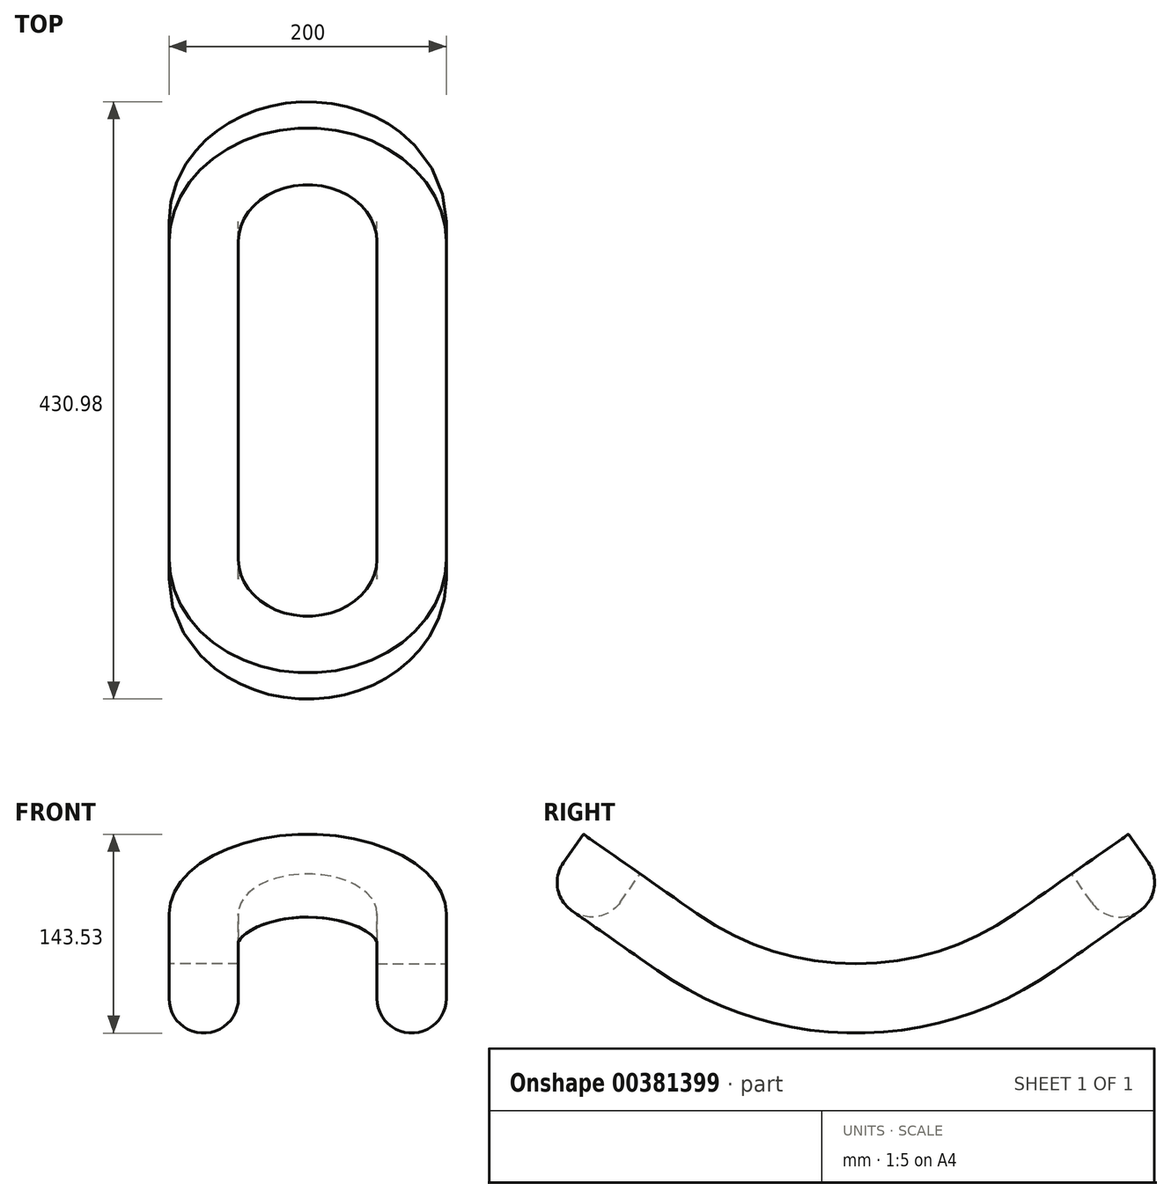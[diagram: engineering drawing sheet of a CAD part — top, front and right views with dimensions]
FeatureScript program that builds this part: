
annotation { "Feature Type Name" : "Feature", "Feature Type Description" : "" }
export const myFeature = defineFeature(function(context is Context, id is Id, definition is map)
    precondition{}
    {
        {
            var Q0;
            Q0=qCreatedBy(makeId("Right.planeOp"),FACE);
            var sketch = newSketch(context, id + "F0", { "sketchPlane" : qUnion([Q0])});
            skLineSegment(sketch, "E0", {"start": v(0, 0) * mm, "end": v(0, 200) * mm, "construction": true});
            skArc(sketch, "E1", {"start": v(0, 0) * mm, "mid": v(60.14, 9.26) * mm, "end": v(114.72, 36.17) * mm});
            skLineSegment(sketch, "E2", {"start": v(114.72, 36.17) * mm, "end": v(196.63, 93.53) * mm});
            skLineSegment(sketch, "E3", {"start": v(114.72, 36.17) * mm, "end": v(0, 200) * mm, "construction": true});
            skSolve(sketch);
        }
        {
            var Q0;
            Q0=sQuery(id+"F0.wireOp",EDGE,"E2");
            var Q1;
            Q1=sQuery(id+"F0.wireOp",EDGE,"E1");
            extrude(context, id + "F1", {"bodyType" : ToolBodyType.SURFACE, "surfaceEntities" : qUnion([Q0, Q1]), "depth" : 100 * mm});
        }
        {
            var Q0;
            Q0=makeQuery(id+"F1.opExtrude","SWEPT_FACE",FACE,{"disambiguationData":[OSD([sQuery(id+"F0.wireOp",EDGE,"E2")])]});
            var sketch = newSketch(context, id + "F2", { "sketchPlane" : qUnion([Q0])});
            skArc(sketch, "E4", {"start": v(0, -214.72) * mm, "mid": v(70.71, -185.43) * mm, "end": v(100, -114.72) * mm});
            skSolve(sketch);
        }
        {
            var Q0;
            Q0=qCreatedBy(makeId("Front.planeOp"),FACE);
            var sketch = newSketch(context, id + "F3", { "sketchPlane" : qUnion([Q0])});
            skLineSegment(sketch, "E5.bottom", {"start": v(50, 0) * mm, "end": v(100, 0) * mm});
            skLineSegment(sketch, "E5.top", {"start": v(50, -25) * mm, "end": v(100, -25) * mm, "construction": true});
            skLineSegment(sketch, "E5.left", {"start": v(50, 0) * mm, "end": v(50, -25) * mm});
            skLineSegment(sketch, "E5.right", {"start": v(100, 0) * mm, "end": v(100, -25) * mm});
            skArc(sketch, "E6", {"start": v(50, -25) * mm, "mid": v(75, -50) * mm, "end": v(100, -25) * mm});
            skSolve(sketch);
        }
        {
            var Q0;
            Q0=makeQuery(id+"F3.imprint","IMPRINT",FACE,{"disambiguationData":[TD([[makeQuery(id+"F3.imprint","IMPRINT",EDGE,{"derivedFrom":sQuery(id+"F3.wireOp",EDGE,"E5.bottom")}),-1.0]])]});
            var Q1;
            Q1=sQuery(id+"F2.wireOp",EDGE,"E4");
            var Q2;
            Q2=makeQuery(id+"F1.opExtrude","CAP_EDGE",EDGE,{"disambiguationData":[OSD([sQuery(id+"F0.wireOp",EDGE,"E1")])],"isStart":false});
            sweep(context, id + "F4", {"profiles" : qUnion([Q0]), "path" : qUnion([Q1, Q2])});
        }
        {
            var Q0;
            Q0=makeQuery(id+"F4.opSweep","SWEPT_BODY",BODY,{"disambiguationData":[OSD([sQuery(id+"F0.wireOp",EDGE,"E1"),sQuery(id+"F3.wireOp",EDGE,"E5.bottom"),sQuery(id+"F3.wireOp",EDGE,"E5.left"),sQuery(id+"F3.wireOp",EDGE,"E5.right"),sQuery(id+"F3.wireOp",EDGE,"E6")])]});
            var Q1;
            Q1=qCreatedBy(makeId("Right.planeOp"),FACE);
            mirror(context, id + "F5", {"operationType" : NewBodyOperationType.ADD, "entities" : qUnion([Q0]), "mirrorPlane" : qUnion([Q1])});
        }
        {
            var Q0;
            Q0=makeQuery(id+"F4.opSweep","SWEPT_BODY",BODY,{"disambiguationData":[OSD([sQuery(id+"F0.wireOp",EDGE,"E1"),sQuery(id+"F3.wireOp",EDGE,"E5.bottom"),sQuery(id+"F3.wireOp",EDGE,"E5.left"),sQuery(id+"F3.wireOp",EDGE,"E5.right"),sQuery(id+"F3.wireOp",EDGE,"E6")])]});
            var Q1;
            Q1=qCreatedBy(makeId("Front.planeOp"),FACE);
            mirror(context, id + "F6", {"operationType" : NewBodyOperationType.ADD, "entities" : qUnion([Q0]), "mirrorPlane" : qUnion([Q1])});
        }
    });
